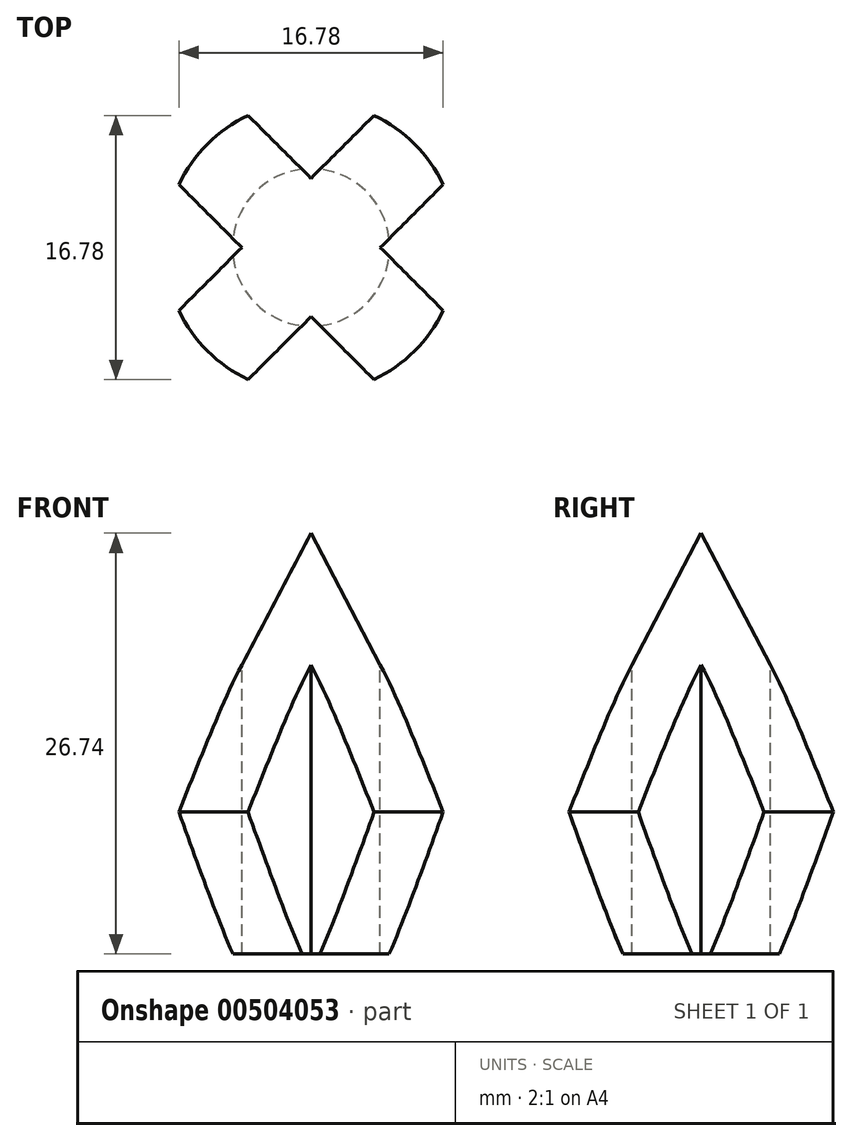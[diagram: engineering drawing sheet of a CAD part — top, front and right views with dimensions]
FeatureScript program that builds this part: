
annotation { "Feature Type Name" : "Feature", "Feature Type Description" : "" }
export const myFeature = defineFeature(function(context is Context, id is Id, definition is map)
    precondition{}
    {
        {
            var Q0;
            Q0=qCreatedBy(makeId("Front.planeOp"),FACE);
            var sketch = newSketch(context, id + "F0", { "sketchPlane" : qUnion([Q0])});
            skLineSegment(sketch, "E0", {"start": v(9.3, 9.03) * mm, "end": v(0, 26.74) * mm});
            skLineSegment(sketch, "E1", {"start": v(0, 0) * mm, "end": v(0, 26.74) * mm});
            skLineSegment(sketch, "E2", {"start": v(0, 0) * mm, "end": v(0, -8.82) * mm, "construction": true});
            skLineSegment(sketch, "E3", {"start": v(9.3, 9.03) * mm, "end": v(5, 0) * mm});
            skLineSegment(sketch, "E4", {"start": v(5, 0) * mm, "end": v(0, 0) * mm});
            skSolve(sketch);
        }
        {
            var Q0;
            Q0=makeQuery(id+"F0.imprint","IMPRINT",FACE,{"disambiguationData":[TD([[makeQuery(id+"F0.imprint","IMPRINT",EDGE,{"derivedFrom":sQuery(id+"F0.wireOp",EDGE,"E0")}),1.0]])]});
            var Q1;
            Q1=sQuery(id+"F0.wireOp",EDGE,"E2");
            revolve(context, id + "F1", {"entities" : qUnion([Q0]), "axis" : qUnion([Q1]), "revolveType" : RevolveType.FULL});
        }
        {
            var Q0;
            Q0=qCreatedBy(makeId("Top.planeOp"),FACE);
            var Q1;
            Q1=makeQuery(id+"F1.opRevolve","SWEPT_VERTEX",VERTEX,{"disambiguationData":[OSD([sQuery(id+"F0.wireOp",EDGE,"E0"),sQuery(id+"F0.wireOp",EDGE,"E1")])]});
            cPlane(context, id + "F2", {"entities" : qUnion([Q0, Q1]), "cplaneType" : CPlaneType.PLANE_POINT, "offset" : 25 * mm, "width" : 150 * mm, "height" : 150 * mm});
        }
        {
            var Q0;
            Q0=qCreatedBy(id+"F2.planeOp",FACE);
            var sketch = newSketch(context, id + "F3", { "sketchPlane" : qUnion([Q0])});
            skLineSegment(sketch, "E5", {"start": v(-4, 8.4) * mm, "end": v(0, 4.4) * mm});
            skLineSegment(sketch, "E6", {"start": v(0, 4.4) * mm, "end": v(4, 8.4) * mm});
            skLineSegment(sketch, "E7", {"start": v(8.4, 4) * mm, "end": v(4.4, 0) * mm});
            skLineSegment(sketch, "E8", {"start": v(4.4, 0) * mm, "end": v(8.4, -4) * mm});
            skLineSegment(sketch, "E9", {"start": v(4, -8.4) * mm, "end": v(0, -4.4) * mm});
            skLineSegment(sketch, "E10", {"start": v(0, -4.4) * mm, "end": v(-4, -8.4) * mm});
            skLineSegment(sketch, "E11", {"start": v(-8.4, 4) * mm, "end": v(-4.4, 0) * mm});
            skLineSegment(sketch, "E12", {"start": v(-4.4, 0) * mm, "end": v(-8.4, -4) * mm});
            skCircle(sketch, "E13", {"center": v(0, 0) * mm, "radius": 9.3 * mm});
            skSolve(sketch);
        }
        {
            var Q0;
            {var subQ0=sQuery(id+"F3.wireOp",EDGE,"E7");Q0=makeQuery(id+"F3.imprint","IMPRINT",FACE,{"disambiguationData":[TD([[makeQuery(id+"F3.imprint","IMPRINT",EDGE,{"derivedFrom":subQ0}),1.0]])]});}
            var Q1;
            {var subQ0=sQuery(id+"F3.wireOp",EDGE,"E5");Q1=makeQuery(id+"F3.imprint","IMPRINT",FACE,{"disambiguationData":[TD([[makeQuery(id+"F3.imprint","IMPRINT",EDGE,{"derivedFrom":subQ0}),1.0]])]});}
            var Q2;
            {var subQ0=sQuery(id+"F3.wireOp",EDGE,"E11");Q2=makeQuery(id+"F3.imprint","IMPRINT",FACE,{"disambiguationData":[TD([[makeQuery(id+"F3.imprint","IMPRINT",EDGE,{"derivedFrom":subQ0}),-1.0]])]});}
            var Q3;
            {var subQ0=sQuery(id+"F3.wireOp",EDGE,"E9");Q3=makeQuery(id+"F3.imprint","IMPRINT",FACE,{"disambiguationData":[TD([[makeQuery(id+"F3.imprint","IMPRINT",EDGE,{"derivedFrom":subQ0}),1.0]])]});}
            extrude(context, id + "F4", {"entities" : qUnion([Q0, Q1, Q2, Q3]), "operationType" : NewBodyOperationType.REMOVE, "endBound" : BoundingType.THROUGH_ALL, "oppositeDirection" : true, "depth" : 25 * mm});
        }
    });
